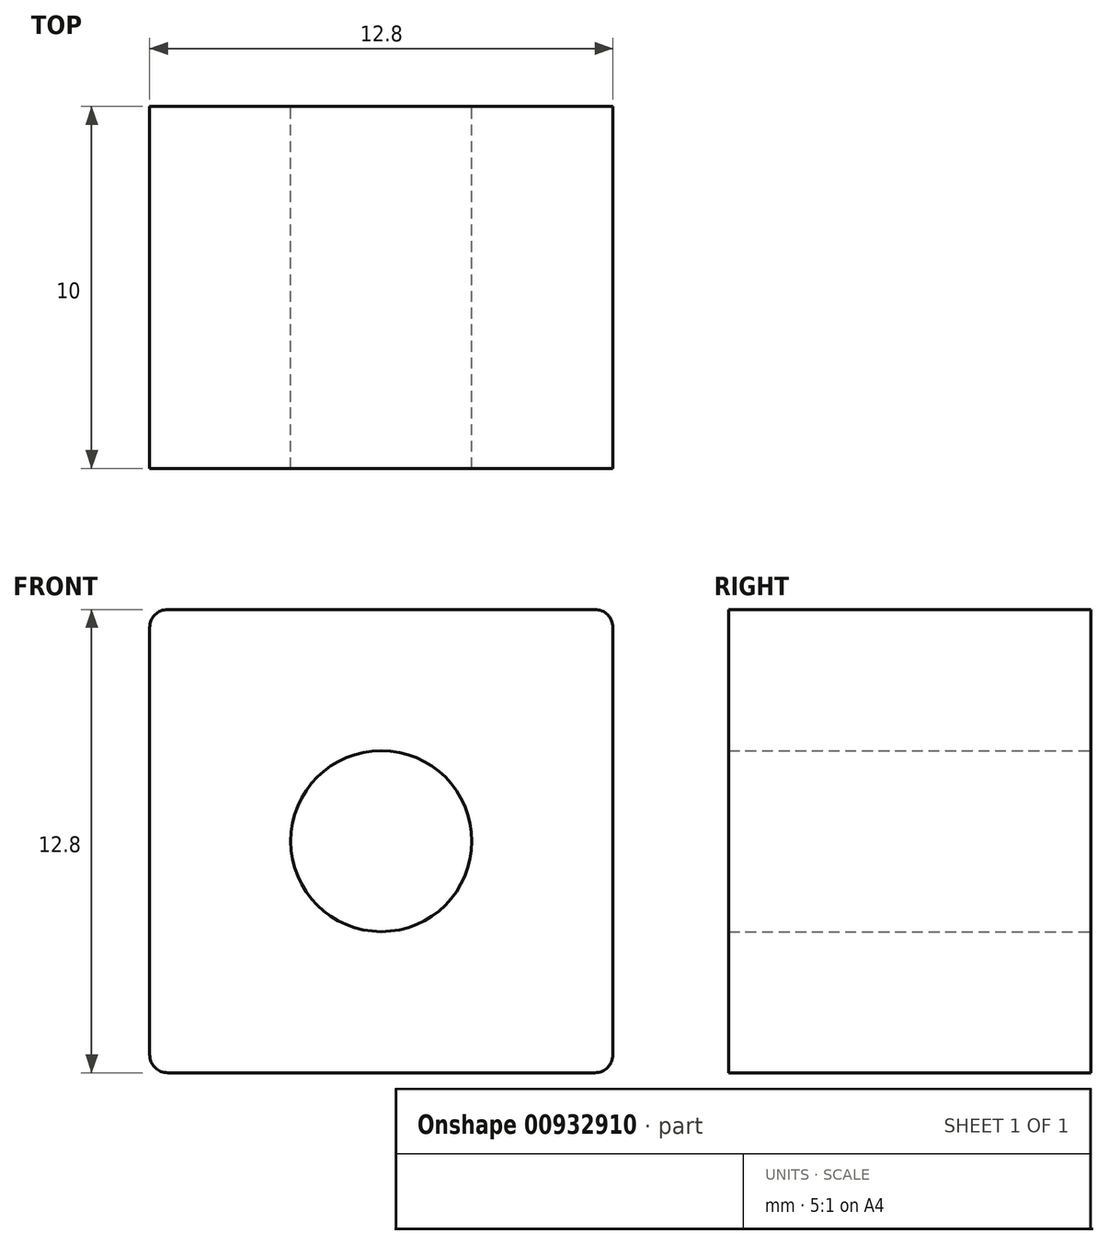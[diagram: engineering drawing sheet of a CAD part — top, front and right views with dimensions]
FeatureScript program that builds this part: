
annotation { "Feature Type Name" : "Feature", "Feature Type Description" : "" }
export const myFeature = defineFeature(function(context is Context, id is Id, definition is map)
    precondition{}
    {
        {
            var Q0;
            Q0=qCreatedBy(makeId("Front.planeOp"),FACE);
            var sketch = newSketch(context, id + "F0", { "sketchPlane" : qUnion([Q0])});
            skLineSegment(sketch, "E0.bottom", {"start": v(0, 0) * mm, "end": v(12.8, 0) * mm});
            skLineSegment(sketch, "E0.top", {"start": v(0, 12.8) * mm, "end": v(12.8, 12.8) * mm});
            skLineSegment(sketch, "E0.left", {"start": v(0, 0) * mm, "end": v(0, 12.8) * mm});
            skLineSegment(sketch, "E0.right", {"start": v(12.8, 0) * mm, "end": v(12.8, 12.8) * mm});
            skCircle(sketch, "E1", {"center": v(6.4, 6.4) * mm, "radius": 2.5 * mm});
            skPoint(sketch, "E1.centerSnap0", {"position": v(0, 6.4) * mm});
            skPoint(sketch, "E1.centerSnap1", {"position": v(6.4, 12.8) * mm});
            skSolve(sketch);
        }
        {
            var Q0;
            Q0 = qSketchRegion(id + "F0", true);
            extrude(context, id + "F1", {"entities" : qUnion([Q0]), "depth" : 10 * mm, "offsetDistance" : 25 * mm});
        }
        {
            var Q0;
            Q0=makeQuery(id+"F1.opExtrude","SWEPT_EDGE",EDGE,{"disambiguationData":[OSD([sQuery(id+"F0.wireOp",EDGE,"E0.top"),sQuery(id+"F0.wireOp",EDGE,"E0.left")])]});
            var Q1;
            Q1=makeQuery(id+"F1.opExtrude","SWEPT_EDGE",EDGE,{"disambiguationData":[OSD([sQuery(id+"F0.wireOp",EDGE,"E0.top"),sQuery(id+"F0.wireOp",EDGE,"E0.right")])]});
            var Q2;
            Q2=makeQuery(id+"F1.opExtrude","SWEPT_EDGE",EDGE,{"disambiguationData":[OSD([sQuery(id+"F0.wireOp",EDGE,"E0.bottom"),sQuery(id+"F0.wireOp",EDGE,"E0.right")])]});
            var Q3;
            Q3=makeQuery(id+"F1.opExtrude","SWEPT_EDGE",EDGE,{"disambiguationData":[OSD([sQuery(id+"F0.wireOp",EDGE,"E0.bottom"),sQuery(id+"F0.wireOp",EDGE,"E0.left")])]});
            fillet(context, id + "F2", {"entities" : qUnion([Q0, Q1, Q2, Q3]), "radius" : .5 * mm, "tangentPropagation" : true, "allowEdgeOverflow" : false});
        }
    });
